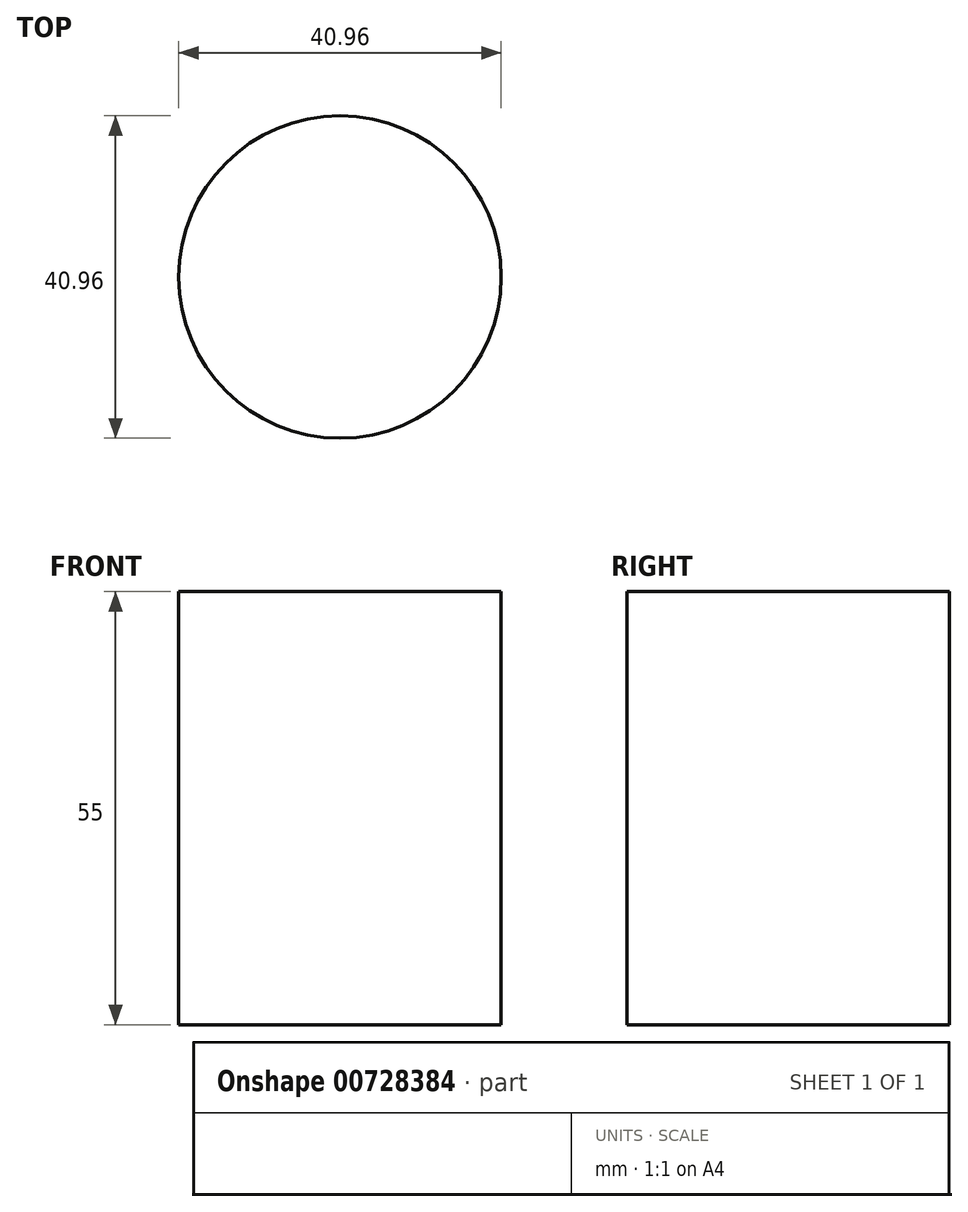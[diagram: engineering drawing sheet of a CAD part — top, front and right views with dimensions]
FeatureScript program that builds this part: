
annotation { "Feature Type Name" : "Feature", "Feature Type Description" : "" }
export const myFeature = defineFeature(function(context is Context, id is Id, definition is map)
    precondition{}
    {
        {
            var Q0;
            Q0=qCreatedBy(makeId("Top.planeOp"),FACE);
            var sketch = newSketch(context, id + "F0", { "sketchPlane" : qUnion([Q0])});
            skCircle(sketch, "E0", {"center": v(0, 0) * mm, "radius": 20.48 * mm});
            skSolve(sketch);
        }
        {
            var Q0;
            Q0=makeQuery(id+"F0.imprint","IMPRINT",FACE,{"disambiguationData":[TD([[makeQuery(id+"F0.imprint","IMPRINT",EDGE,{"derivedFrom":sQuery(id+"F0.wireOp",EDGE,"E0")}),1.0]])]});
            extrude(context, id + "F1", {"entities" : qUnion([Q0]), "depth" : 55 * mm, "offsetDistance" : 25 * mm});
        }
    });
